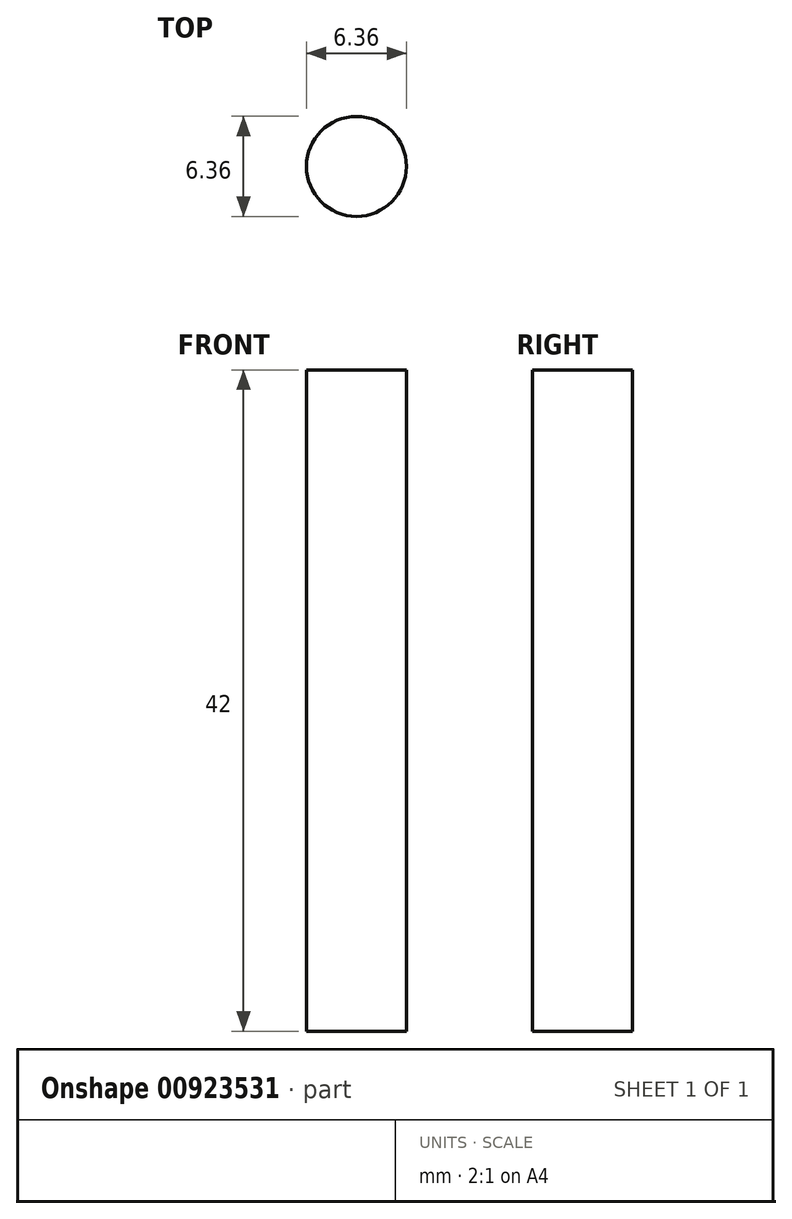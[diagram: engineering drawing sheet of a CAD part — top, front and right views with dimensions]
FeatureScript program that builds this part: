
annotation { "Feature Type Name" : "Feature", "Feature Type Description" : "" }
export const myFeature = defineFeature(function(context is Context, id is Id, definition is map)
    precondition{}
    {
        {
            var Q0;
            Q0=qCreatedBy(makeId("Top.planeOp"),FACE);
            var sketch = newSketch(context, id + "F0", { "sketchPlane" : qUnion([Q0])});
            skCircle(sketch, "E0", {"center": v(0, 0) * mm, "radius": 3.18 * mm});
            skSolve(sketch);
        }
        {
            var Q0;
            Q0=makeQuery(id+"F0.imprint","IMPRINT",FACE,{"disambiguationData":[TD([[makeQuery(id+"F0.imprint","IMPRINT",EDGE,{"derivedFrom":sQuery(id+"F0.wireOp",EDGE,"E0")}),1.0]])]});
            extrude(context, id + "F1", {"entities" : qUnion([Q0]), "depth" : 42 * mm, "offsetDistance" : 25.4 * mm});
        }
    });
